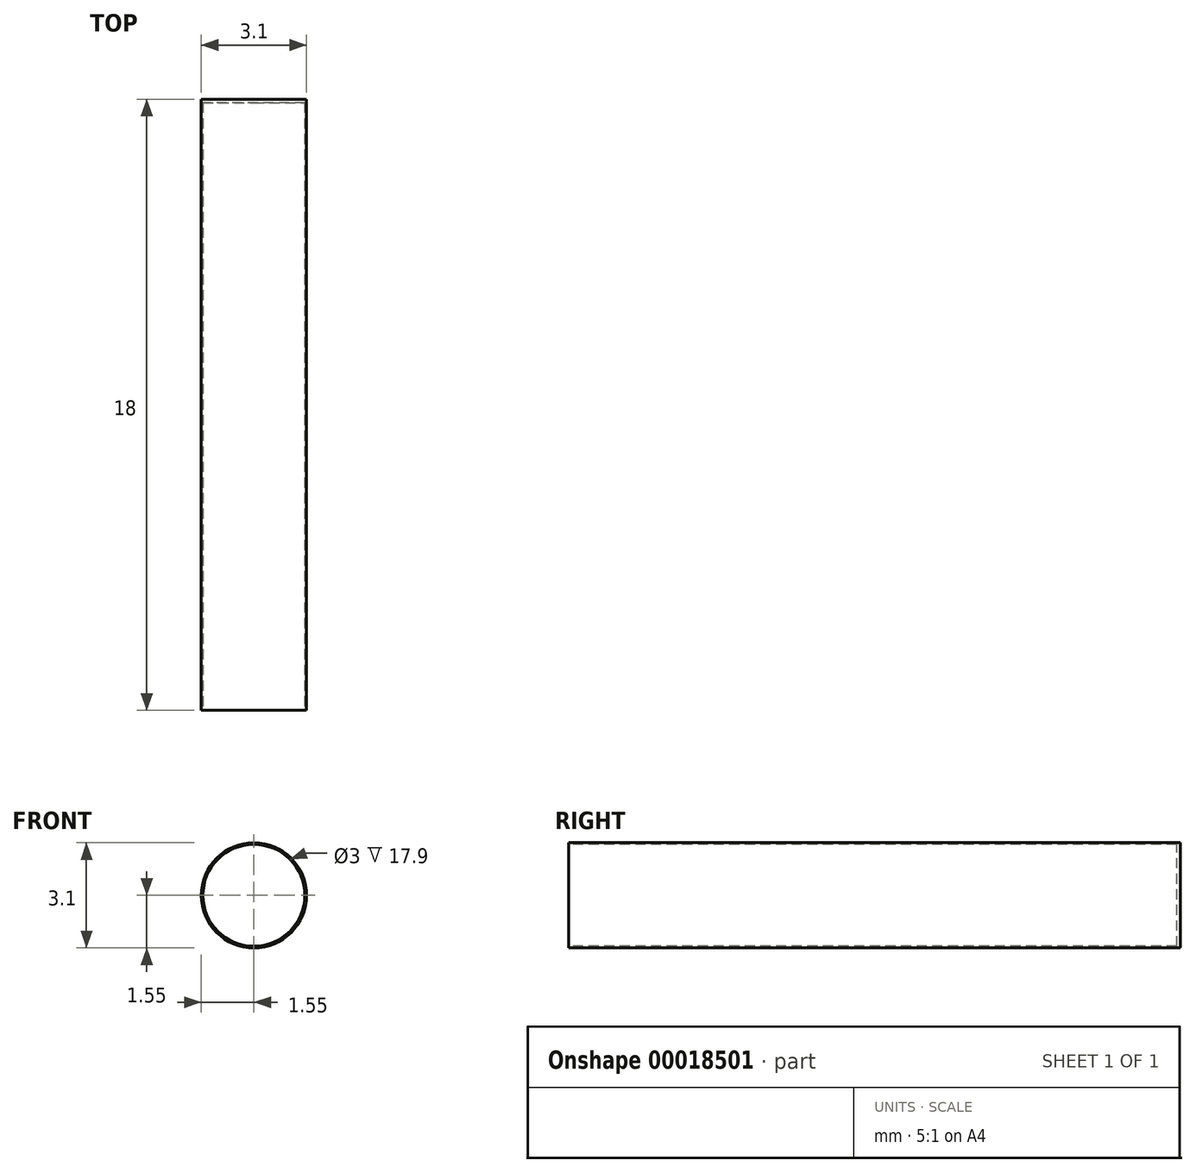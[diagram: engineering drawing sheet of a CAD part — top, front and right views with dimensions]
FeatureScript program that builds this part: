
annotation { "Feature Type Name" : "Feature", "Feature Type Description" : "" }
export const myFeature = defineFeature(function(context is Context, id is Id, definition is map)
    precondition{}
    {
        {
            var Q0;
            Q0=qCreatedBy(makeId("Front.planeOp"),FACE);
            var sketch = newSketch(context, id + "F0", { "sketchPlane" : qUnion([Q0])});
            skCircle(sketch, "E0", {"center": v(0, 0) * mm, "radius": 1.55 * mm});
            skSolve(sketch);
        }
        {
            var Q0;
            Q0 = qSketchRegion(id + "F0", true);
            extrude(context, id + "F1", {"entities" : qUnion([Q0]), "depth" : 18 * mm});
        }
        {
            var Q0;
            Q0=makeQuery(id+"F1.opExtrude","CAP_FACE",FACE,{"disambiguationData":[OSD([sQuery(id+"F0.wireOp",EDGE,"E0")])],"isStart":false});
            var sketch = newSketch(context, id + "F2", { "sketchPlane" : qUnion([Q0])});
            skCircle(sketch, "E1", {"center": v(0, 0) * mm, "radius": 1.5 * mm});
            skSolve(sketch);
        }
        {
            var Q0;
            Q0=makeQuery(id+"F2.imprint","IMPRINT",FACE,{"disambiguationData":[TD([[makeQuery(id+"F2.imprint","IMPRINT",EDGE,{"derivedFrom":sQuery(id+"F2.wireOp",EDGE,"E1")}),1.0]])]});
            extrude(context, id + "F3", {"entities" : qUnion([Q0]), "operationType" : NewBodyOperationType.REMOVE, "oppositeDirection" : true, "depth" : 17.9 * mm});
        }
    });
